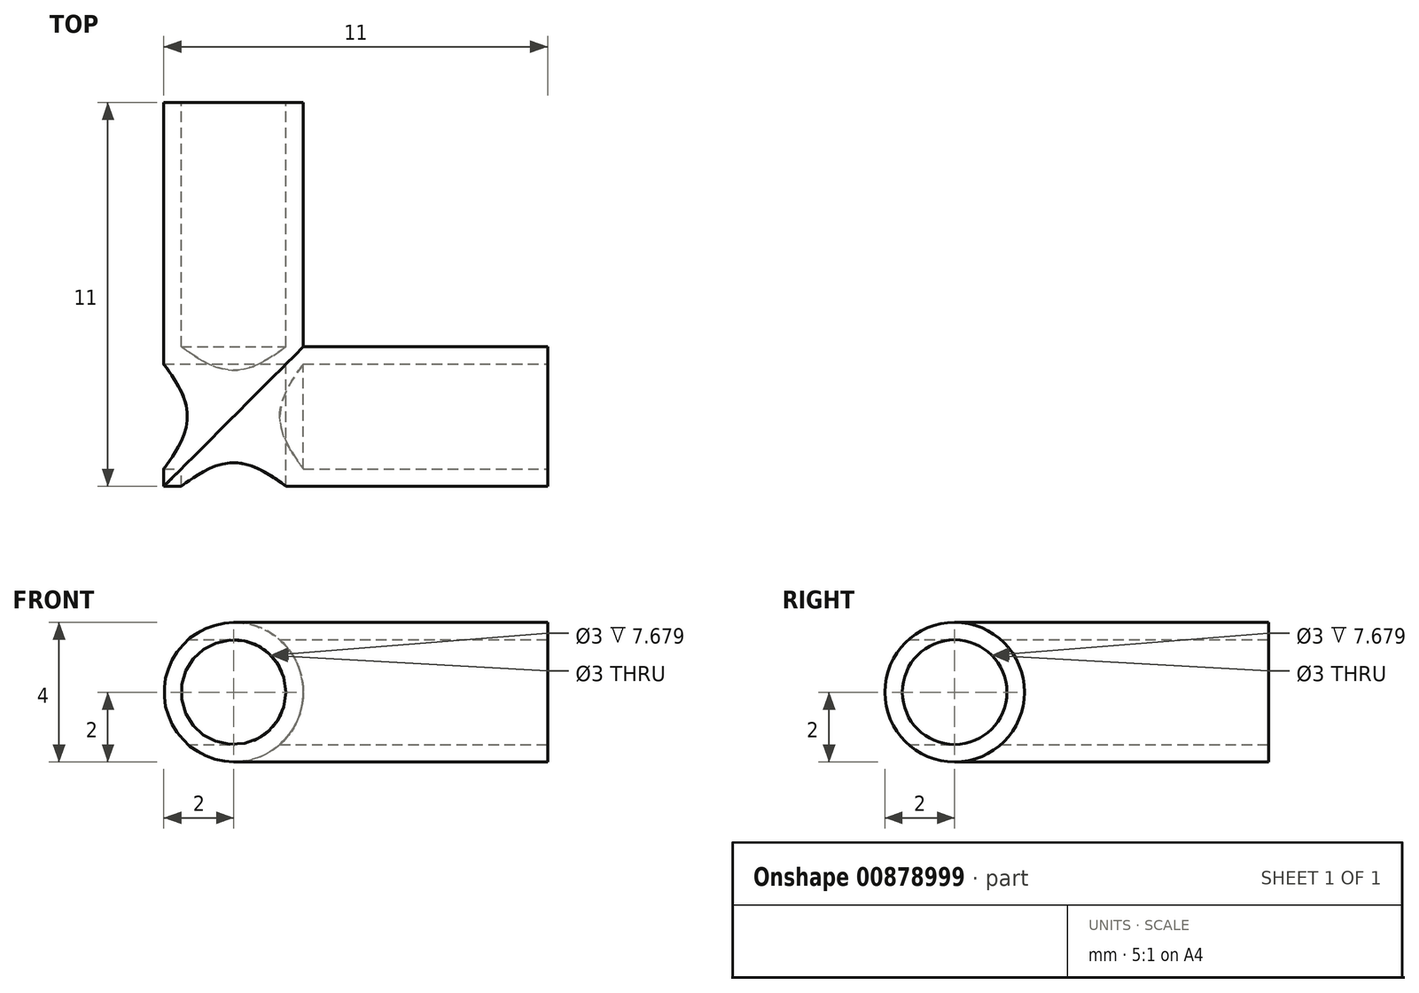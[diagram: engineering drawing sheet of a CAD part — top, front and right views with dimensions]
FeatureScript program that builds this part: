
annotation { "Feature Type Name" : "Feature", "Feature Type Description" : "" }
export const myFeature = defineFeature(function(context is Context, id is Id, definition is map)
    precondition{}
    {
        {
            var Q0;
            Q0=qCreatedBy(makeId("Front.planeOp"),FACE);
            var sketch = newSketch(context, id + "F0", { "sketchPlane" : qUnion([Q0])});
            skLineSegment(sketch, "E0.bottom", {"start": v(0, 0) * mm, "end": v(-9, 0) * mm, "construction": true});
            skLineSegment(sketch, "E0.top", {"start": v(0, 9) * mm, "end": v(-9, 9) * mm, "construction": true});
            skLineSegment(sketch, "E0.left", {"start": v(0, 0) * mm, "end": v(0, 9) * mm, "construction": true});
            skLineSegment(sketch, "E0.right", {"start": v(-9, 0) * mm, "end": v(-9, 9) * mm, "construction": true});
            skCircle(sketch, "E1", {"center": v(-9, 9) * mm, "radius": 2 * mm});
            skCircle(sketch, "E2", {"center": v(-9, 9) * mm, "radius": 1.5 * mm});
            skLineSegment(sketch, "E3", {"start": v(-9, 7) * mm, "end": v(-9, 11) * mm});
            skSolve(sketch);
        }
        {
            var Q0;
            Q0 = qSketchRegion(id + "F0", true);
            extrude(context, id + "F1", {"entities" : qUnion([Q0]), "depth" : 11 * mm, "offsetDistance" : 25 * mm});
        }
        {
            var Q0;
            Q0=qCreatedBy(makeId("Right.planeOp"),FACE);
            var sketch = newSketch(context, id + "F2", { "sketchPlane" : qUnion([Q0])});
            skLineSegment(sketch, "E4.bottom", {"start": v(0, 0) * mm, "end": v(-9, 0) * mm, "construction": true});
            skLineSegment(sketch, "E4.top", {"start": v(0, 9) * mm, "end": v(-9, 9) * mm, "construction": true});
            skLineSegment(sketch, "E4.left", {"start": v(0, 0) * mm, "end": v(0, 9) * mm, "construction": true});
            skLineSegment(sketch, "E4.right", {"start": v(-9, 0) * mm, "end": v(-9, 9) * mm, "construction": true});
            skCircle(sketch, "E5", {"center": v(-9, 9) * mm, "radius": 2 * mm});
            skCircle(sketch, "E6", {"center": v(-9, 9) * mm, "radius": 1.5 * mm});
            skLineSegment(sketch, "E7", {"start": v(-9, 7) * mm, "end": v(-9, 11) * mm});
            skSolve(sketch);
        }
        {
            var Q0;
            Q0=makeQuery(id+"F2.imprint","IMPRINT",FACE,{"disambiguationData":[TD([[makeQuery(id+"F2.imprint","IMPRINT",EDGE,{"derivedFrom":sQuery(id+"F2.wireOp",EDGE,"E5")}),1.0]])]});
            var Q1;
            Q1=sQuery(id+"F2.wireOp",EDGE,"E5");
            extrude(context, id + "F3", {"entities" : qUnion([Q0]), "operationType" : NewBodyOperationType.INTERSECT, "surfaceEntities" : qUnion([Q1]), "oppositeDirection" : true, "depth" : 11 * mm, "offsetDistance" : 25 * mm});
        }
        {
            var Q0;
            Q0=makeQuery(id+"F0.imprint","IMPRINT",FACE,{"disambiguationData":[TD([[makeQuery(id+"F0.imprint","IMPRINT",EDGE,{"derivedFrom":sQuery(id+"F0.wireOp",EDGE,"E1")}),1.0]])]});
            extrude(context, id + "F4", {"entities" : qUnion([Q0]), "operationType" : NewBodyOperationType.ADD, "depth" : 7.5 * mm, "offsetDistance" : 25 * mm});
        }
        {
            var Q0;
            Q0=makeQuery(id+"F4.boolean.opBoolean","SPLIT",FACE,{"disambiguationData":[OD(1.0)],"derivedFrom":makeQuery(id+"F4.opExtrude","CAP_FACE",FACE,{"disambiguationData":[OSD([sQuery(id+"F0.wireOp",EDGE,"E1"),sQuery(id+"F0.wireOp",EDGE,"E2")])],"isStart":false})});
            extrude(context, id + "F5", {"entities" : qUnion([Q0]), "operationType" : NewBodyOperationType.ADD, "depth" : 0.75 * mm, "offsetDistance" : 25 * mm});
        }
        {
            var Q0;
            Q0=makeQuery(id+"F5.opExtrude","CAP_FACE",FACE,{"disambiguationData":[OSD([sQuery(id+"F0.wireOp",EDGE,"E1"),sQuery(id+"F0.wireOp",EDGE,"E2")])],"isStart":false});
            extrude(context, id + "F6", {"entities" : qUnion([Q0]), "operationType" : NewBodyOperationType.ADD, "depth" : 0.75 * mm, "offsetDistance" : 25 * mm});
        }
        {
            var Q0;
            Q0=makeQuery(id+"F2.imprint","IMPRINT",FACE,{"disambiguationData":[TD([[makeQuery(id+"F2.imprint","IMPRINT",EDGE,{"derivedFrom":sQuery(id+"F2.wireOp",EDGE,"E5")}),1.0]])]});
            extrude(context, id + "F7", {"entities" : qUnion([Q0]), "operationType" : NewBodyOperationType.ADD, "oppositeDirection" : true, "depth" : 7.5 * mm, "offsetDistance" : 25 * mm});
        }
        {
            var Q0;
            {var subQ0=sQuery(id+"F2.wireOp",EDGE,"E6");var subQ1=sQuery(id+"F2.wireOp",EDGE,"E5");var subQ2=sQuery(id+"F0.wireOp",EDGE,"E1");Q0=makeQuery(id+"F7.boolean.opBoolean","SPLIT",FACE,{"disambiguationData":[TD([makeQuery(id+"F1.opExtrude","SWEPT_FACE",FACE,{"disambiguationData":[OSD([subQ2])]}),makeQuery(id+"F3.boolean.opBoolean","COPY",FACE,{"disambiguationData":[OD(0.0)],"derivedFrom":makeQuery(id+"F3.boolean.toolComplement.opBoolean","COPY",FACE,{"derivedFrom":makeQuery(id+"F3.opExtrude","SWEPT_FACE",FACE,{"disambiguationData":[OSD([subQ1])]})})}),makeQuery(id+"F3.boolean.opBoolean","COPY",FACE,{"disambiguationData":[OD(1.0)],"derivedFrom":makeQuery(id+"F3.boolean.toolComplement.opBoolean","COPY",FACE,{"derivedFrom":makeQuery(id+"F3.opExtrude","SWEPT_FACE",FACE,{"disambiguationData":[OSD([subQ0])]})})}),makeQuery(id+"F4.opExtrude","SWEPT_FACE",FACE,{"disambiguationData":[OSD([subQ2])]}),makeQuery(id+"F5.opExtrude","SWEPT_FACE",FACE,{"disambiguationData":[OSD([subQ2])]}),makeQuery(id+"F6.opExtrude","SWEPT_FACE",FACE,{"disambiguationData":[OSD([subQ2])]}),makeQuery(id+"F7.opExtrude","SWEPT_FACE",FACE,{"disambiguationData":[OSD([subQ1])]}),makeQuery(id+"F7.opExtrude","SWEPT_FACE",FACE,{"disambiguationData":[OSD([subQ0])]})])],"derivedFrom":makeQuery(id+"F7.opExtrude","CAP_FACE",FACE,{"disambiguationData":[OSD([subQ1,subQ0])],"isStart":false})});}
            extrude(context, id + "F8", {"entities" : qUnion([Q0]), "operationType" : NewBodyOperationType.ADD, "depth" : 0.75 * mm, "offsetDistance" : 25 * mm});
        }
        {
            var Q0;
            Q0=makeQuery(id+"F8.opExtrude","CAP_FACE",FACE,{"disambiguationData":[OSD([sQuery(id+"F2.wireOp",EDGE,"E5"),sQuery(id+"F2.wireOp",EDGE,"E6")])],"isStart":false});
            extrude(context, id + "F9", {"entities" : qUnion([Q0]), "operationType" : NewBodyOperationType.ADD, "depth" : 0.75 * mm, "offsetDistance" : 25 * mm});
        }
        {
            var Q0;
            {var subQ0=sQuery(id+"F2.wireOp",EDGE,"E6");var subQ1=sQuery(id+"F2.wireOp",EDGE,"E5");var subQ2=makeQuery(id+"F3.boolean.toolComplement.opBoolean","COPY",FACE,{"derivedFrom":makeQuery(id+"F3.opExtrude","SWEPT_FACE",FACE,{"disambiguationData":[OSD([subQ1])]})});var subQ3=sQuery(id+"F0.wireOp",EDGE,"E1");Q0=makeQuery(id+"F7.boolean.opBoolean","SPLIT",FACE,{"disambiguationData":[TD([makeQuery(id+"F1.opExtrude","SWEPT_FACE",FACE,{"disambiguationData":[OSD([subQ3])]}),makeQuery(id+"F3.boolean.opBoolean","COPY",FACE,{"disambiguationData":[OD(0.0)],"derivedFrom":subQ2}),makeQuery(id+"F3.boolean.opBoolean","COPY",FACE,{"disambiguationData":[OD(1.0)],"derivedFrom":subQ2}),makeQuery(id+"F3.boolean.opBoolean","COPY",FACE,{"disambiguationData":[OD(1.0)],"derivedFrom":makeQuery(id+"F3.boolean.toolComplement.opBoolean","COPY",FACE,{"derivedFrom":makeQuery(id+"F3.opExtrude","SWEPT_FACE",FACE,{"disambiguationData":[OSD([subQ0])]})})}),makeQuery(id+"F4.opExtrude","SWEPT_FACE",FACE,{"disambiguationData":[OSD([subQ3])]}),makeQuery(id+"F4.opExtrude","CAP_FACE",FACE,{"disambiguationData":[OSD([subQ3,sQuery(id+"F0.wireOp",EDGE,"E2")])],"isStart":false}),makeQuery(id+"F5.opExtrude","SWEPT_FACE",FACE,{"disambiguationData":[OSD([subQ3])]}),makeQuery(id+"F6.opExtrude","SWEPT_FACE",FACE,{"disambiguationData":[OSD([subQ3])]}),makeQuery(id+"F7.opExtrude","SWEPT_FACE",FACE,{"disambiguationData":[OSD([subQ1])]}),makeQuery(id+"F7.opExtrude","SWEPT_FACE",FACE,{"disambiguationData":[OSD([subQ0])]})])],"derivedFrom":makeQuery(id+"F7.opExtrude","CAP_FACE",FACE,{"disambiguationData":[OSD([subQ1,subQ0])],"isStart":false})});}
            extrude(context, id + "F10", {"entities" : qUnion([Q0]), "operationType" : NewBodyOperationType.ADD, "depth" : 0.75 * mm, "offsetDistance" : 25 * mm});
        }
        {
            var Q0;
            Q0=makeQuery(id+"F10.opExtrude","CAP_FACE",FACE,{"disambiguationData":[OSD([sQuery(id+"F2.wireOp",EDGE,"E5"),sQuery(id+"F2.wireOp",EDGE,"E6")])],"isStart":false});
            extrude(context, id + "F11", {"entities" : qUnion([Q0]), "operationType" : NewBodyOperationType.ADD, "depth" : 0.75 * mm, "offsetDistance" : 25 * mm});
        }
        {
            var Q0;
            Q0=makeQuery(id+"F4.boolean.opBoolean","SPLIT",FACE,{"disambiguationData":[OD(0.0)],"derivedFrom":makeQuery(id+"F4.opExtrude","CAP_FACE",FACE,{"disambiguationData":[OSD([sQuery(id+"F0.wireOp",EDGE,"E1"),sQuery(id+"F0.wireOp",EDGE,"E2")])],"isStart":false})});
            extrude(context, id + "F12", {"entities" : qUnion([Q0]), "operationType" : NewBodyOperationType.ADD, "depth" : 0.75 * mm, "offsetDistance" : 25 * mm});
        }
        {
            var Q0;
            Q0=makeQuery(id+"F12.opExtrude","CAP_FACE",FACE,{"disambiguationData":[OSD([sQuery(id+"F0.wireOp",EDGE,"E1"),sQuery(id+"F0.wireOp",EDGE,"E2")])],"isStart":false});
            extrude(context, id + "F13", {"entities" : qUnion([Q0]), "operationType" : NewBodyOperationType.ADD, "depth" : 0.75 * mm, "offsetDistance" : 25 * mm});
        }
        {
            var Q0;
            {var subQ0=sQuery(id+"F0.wireOp",EDGE,"E3");var subQ1=sQuery(id+"F0.wireOp",EDGE,"E1");var subQ2=makeQuery(id+"F0.imprint","INTERSECT",VERTEX,{"disambiguationData":[OD(0.0)],"derivedFrom":[subQ1,subQ0]});Q0=makeQuery(id+"F0.imprint","IMPRINT",FACE,{"disambiguationData":[TD([[makeQuery(id+"F0.imprint","IMPRINT",EDGE,{"disambiguationData":[TD([[subQ2,1.0]])],"derivedFrom":subQ1}),1.0]])]});}
            extrude(context, id + "F14", {"entities" : qUnion([Q0]), "operationType" : NewBodyOperationType.ADD, "depth" : 9 * mm, "offsetDistance" : 25 * mm});
        }
        {
            var Q0;
            Q0=makeQuery(id+"F14.opExtrude","CAP_FACE",FACE,{"disambiguationData":[OSD([sQuery(id+"F0.wireOp",EDGE,"E1"),sQuery(id+"F0.wireOp",EDGE,"E2"),sQuery(id+"F0.wireOp",EDGE,"E3")])],"isStart":false});
            extrude(context, id + "F15", {"entities" : qUnion([Q0]), "operationType" : NewBodyOperationType.ADD, "depth" : 1 * mm, "offsetDistance" : 25 * mm});
        }
        {
            var Q0;
            Q0=makeQuery(id+"F15.opExtrude","CAP_FACE",FACE,{"disambiguationData":[OSD([sQuery(id+"F0.wireOp",EDGE,"E1"),sQuery(id+"F0.wireOp",EDGE,"E2"),sQuery(id+"F0.wireOp",EDGE,"E3")])],"isStart":false});
            extrude(context, id + "F16", {"entities" : qUnion([Q0]), "operationType" : NewBodyOperationType.ADD, "depth" : 0.53 * mm, "offsetDistance" : 25 * mm});
        }
        {
            var Q0;
            {var subQ0=sQuery(id+"F2.wireOp",EDGE,"E7");var subQ1=sQuery(id+"F2.wireOp",EDGE,"E5");var subQ2=makeQuery(id+"F2.imprint","INTERSECT",VERTEX,{"disambiguationData":[OD(0.0)],"derivedFrom":[subQ1,subQ0]});Q0=makeQuery(id+"F2.imprint","IMPRINT",FACE,{"disambiguationData":[TD([[makeQuery(id+"F2.imprint","IMPRINT",EDGE,{"disambiguationData":[TD([[subQ2,1.0]])],"derivedFrom":subQ1}),1.0]])]});}
            extrude(context, id + "F17", {"entities" : qUnion([Q0]), "operationType" : NewBodyOperationType.ADD, "oppositeDirection" : true, "depth" : 9 * mm, "offsetDistance" : 25 * mm});
        }
        {
            var Q0;
            Q0=makeQuery(id+"F17.opExtrude","CAP_FACE",FACE,{"disambiguationData":[OSD([sQuery(id+"F2.wireOp",EDGE,"E5"),sQuery(id+"F2.wireOp",EDGE,"E6"),sQuery(id+"F2.wireOp",EDGE,"E7")])],"isStart":false});
            extrude(context, id + "F18", {"entities" : qUnion([Q0]), "operationType" : NewBodyOperationType.ADD, "depth" : 1 * mm, "offsetDistance" : 25 * mm});
        }
        {
            var Q0;
            Q0=makeQuery(id+"F18.opExtrude","CAP_FACE",FACE,{"disambiguationData":[OSD([sQuery(id+"F2.wireOp",EDGE,"E5"),sQuery(id+"F2.wireOp",EDGE,"E6"),sQuery(id+"F2.wireOp",EDGE,"E7")])],"isStart":false});
            extrude(context, id + "F19", {"entities" : qUnion([Q0]), "operationType" : NewBodyOperationType.ADD, "depth" : 0.53 * mm, "offsetDistance" : 25 * mm});
        }
    });
